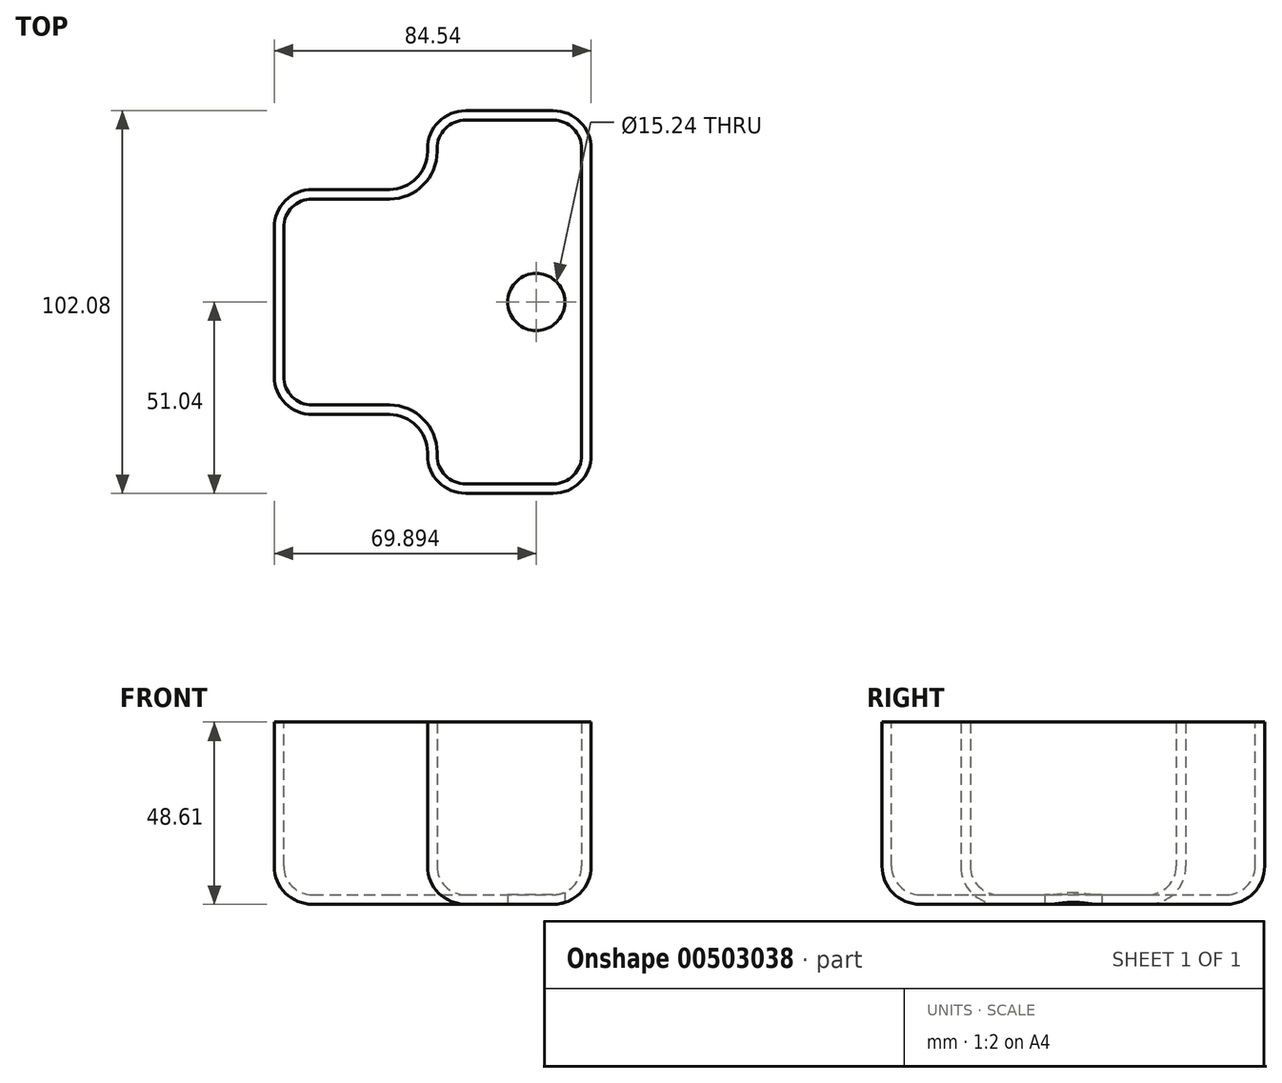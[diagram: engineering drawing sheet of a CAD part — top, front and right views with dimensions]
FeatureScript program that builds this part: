
annotation { "Feature Type Name" : "Feature", "Feature Type Description" : "" }
export const myFeature = defineFeature(function(context is Context, id is Id, definition is map)
    precondition{}
    {
        {
            var Q0;
            Q0=qCreatedBy(makeId("Top.planeOp"),FACE);
            var sketch = newSketch(context, id + "F0", { "sketchPlane" : qUnion([Q0])});
            skLineSegment(sketch, "E0.bottom", {"start": v(0, 51.04) * mm, "end": v(43.66, 51.04) * mm});
            skLineSegment(sketch, "E0.top", {"start": v(0, -51.04) * mm, "end": v(43.66, -51.04) * mm});
            skLineSegment(sketch, "E0.left", {"start": v(0, 51.04) * mm, "end": v(0, -51.04) * mm});
            skLineSegment(sketch, "E0.right", {"start": v(43.66, 51.04) * mm, "end": v(43.66, -51.04) * mm});
            skPoint(sketch, "E0.middle", {"position": v(21.83, 0) * mm});
            skLineSegment(sketch, "E1.bottom", {"start": v(0, -30.01) * mm, "end": v(-40.88, -30.01) * mm});
            skLineSegment(sketch, "E1.top", {"start": v(0, 30.01) * mm, "end": v(-40.88, 30.01) * mm});
            skLineSegment(sketch, "E1.left", {"start": v(0, -30.01) * mm, "end": v(0, 30.01) * mm});
            skLineSegment(sketch, "E1.right", {"start": v(-40.88, -30.01) * mm, "end": v(-40.88, 30.01) * mm});
            skPoint(sketch, "E1.middle", {"position": v(-20.44, 0) * mm});
            skSolve(sketch);
        }
        {
            var Q0;
            Q0=makeQuery(id+"F0.imprint","IMPRINT",FACE,{"disambiguationData":[TD([[makeQuery(id+"F0.imprint","IMPRINT",EDGE,{"derivedFrom":sQuery(id+"F0.wireOp",EDGE,"E0.bottom")}),-1.0]])]});
            var Q1;
            Q1=makeQuery(id+"F0.imprint","IMPRINT",FACE,{"disambiguationData":[TD([[makeQuery(id+"F0.imprint","IMPRINT",EDGE,{"derivedFrom":sQuery(id+"F0.wireOp",EDGE,"E1.bottom")}),-1.0]])]});
            extrude(context, id + "F1", {"entities" : qUnion([Q0, Q1]), "depth" : 48.6 * mm});
        }
        {
            var Q0;
            Q0=makeQuery(id+"F1.opExtrude","SWEPT_EDGE",EDGE,{"disambiguationData":[OSD([sQuery(id+"F0.wireOp",EDGE,"E0.bottom"),sQuery(id+"F0.wireOp",EDGE,"E0.left")])]});
            var Q1;
            Q1=makeQuery(id+"F1.opExtrude","SWEPT_EDGE",EDGE,{"disambiguationData":[OSD([sQuery(id+"F0.wireOp",EDGE,"E0.top"),sQuery(id+"F0.wireOp",EDGE,"E0.right")])]});
            var Q2;
            Q2=makeQuery(id+"F1.opExtrude","SWEPT_EDGE",EDGE,{"disambiguationData":[OSD([sQuery(id+"F0.wireOp",EDGE,"E0.bottom"),sQuery(id+"F0.wireOp",EDGE,"E0.right")])]});
            var Q3;
            Q3=makeQuery(id+"F1.opExtrude","SWEPT_EDGE",EDGE,{"disambiguationData":[OSD([sQuery(id+"F0.wireOp",EDGE,"E0.top"),sQuery(id+"F0.wireOp",EDGE,"E0.left")])]});
            var Q4;
            Q4=makeQuery(id+"F1.opExtrude","CAP_FACE",FACE,{"disambiguationData":[OSD([sQuery(id+"F0.wireOp",EDGE,"E0.bottom"),sQuery(id+"F0.wireOp",EDGE,"E0.top"),sQuery(id+"F0.wireOp",EDGE,"E0.left"),sQuery(id+"F0.wireOp",EDGE,"E0.right")])],"isStart":true});
            var Q5;
            Q5=makeQuery(id+"F1.opExtrude","SWEPT_EDGE",EDGE,{"disambiguationData":[OSD([sQuery(id+"F0.wireOp",EDGE,"E0.left"),sQuery(id+"F0.wireOp",EDGE,"E1.top"),sQuery(id+"F0.wireOp",EDGE,"E1.left")])]});
            var Q6;
            Q6=makeQuery(id+"F1.opExtrude","SWEPT_EDGE",EDGE,{"disambiguationData":[OSD([sQuery(id+"F0.wireOp",EDGE,"E1.top"),sQuery(id+"F0.wireOp",EDGE,"E1.right")])]});
            var Q7;
            Q7=makeQuery(id+"F1.opExtrude","SWEPT_EDGE",EDGE,{"disambiguationData":[OSD([sQuery(id+"F0.wireOp",EDGE,"E1.bottom"),sQuery(id+"F0.wireOp",EDGE,"E1.right")])]});
            var Q8;
            Q8=makeQuery(id+"F1.opExtrude","SWEPT_EDGE",EDGE,{"disambiguationData":[OSD([sQuery(id+"F0.wireOp",EDGE,"E0.left"),sQuery(id+"F0.wireOp",EDGE,"E1.bottom"),sQuery(id+"F0.wireOp",EDGE,"E1.left")])]});
            fillet(context, id + "F2", {"entities" : qUnion([Q0, Q1, Q2, Q3, Q4, Q5, Q6, Q7, Q8]), "radius" : 10.16 * mm, "tangentPropagation" : true, "allowEdgeOverflow" : false});
        }
        {
            var Q0;
            Q0=makeQuery(id+"F1.opExtrude","CAP_FACE",FACE,{"disambiguationData":[OSD([sQuery(id+"F0.wireOp",EDGE,"E0.bottom"),sQuery(id+"F0.wireOp",EDGE,"E0.top"),sQuery(id+"F0.wireOp",EDGE,"E0.left"),sQuery(id+"F0.wireOp",EDGE,"E0.right")])],"isStart":false});
            shell(context, id + "F3", {"entities" : qUnion([Q0]), "thickness" : 2.54 * mm});
        }
        {
            var Q0;
            Q0=qCreatedBy(makeId("Top.planeOp"),FACE);
            var sketch = newSketch(context, id + "F4", { "sketchPlane" : qUnion([Q0])});
            skPoint(sketch, "E2", {"position": v(29.01, 0) * mm});
            skSolve(sketch);
        }
        {
            var Q0;
            Q0=sQuery(id+"F4.wireOp",VERTEX,"E2");
            var Q1;
            Q1=makeQuery(id+"F1.opExtrude","SWEPT_BODY",BODY,{"disambiguationData":[OSD([sQuery(id+"F0.wireOp",EDGE,"E0.bottom"),sQuery(id+"F0.wireOp",EDGE,"E0.top"),sQuery(id+"F0.wireOp",EDGE,"E0.left"),sQuery(id+"F0.wireOp",EDGE,"E0.right"),sQuery(id+"F0.wireOp",EDGE,"E1.bottom"),sQuery(id+"F0.wireOp",EDGE,"E1.top"),sQuery(id+"F0.wireOp",EDGE,"E1.right")])]});
            hole(context, id + "F5", {"style" : HoleStyle.SIMPLE, "endStyle" : HoleEndStyle.THROUGH, "oppositeDirection" : true, "holeDiameter" : 15.24 * mm, "isTappedThrough" : true, "tappedDepth" : 12.7 * mm, "tapClearance" : 3, "locations" : qUnion([Q0]), "scope" : qUnion([Q1])});
        }
    });
